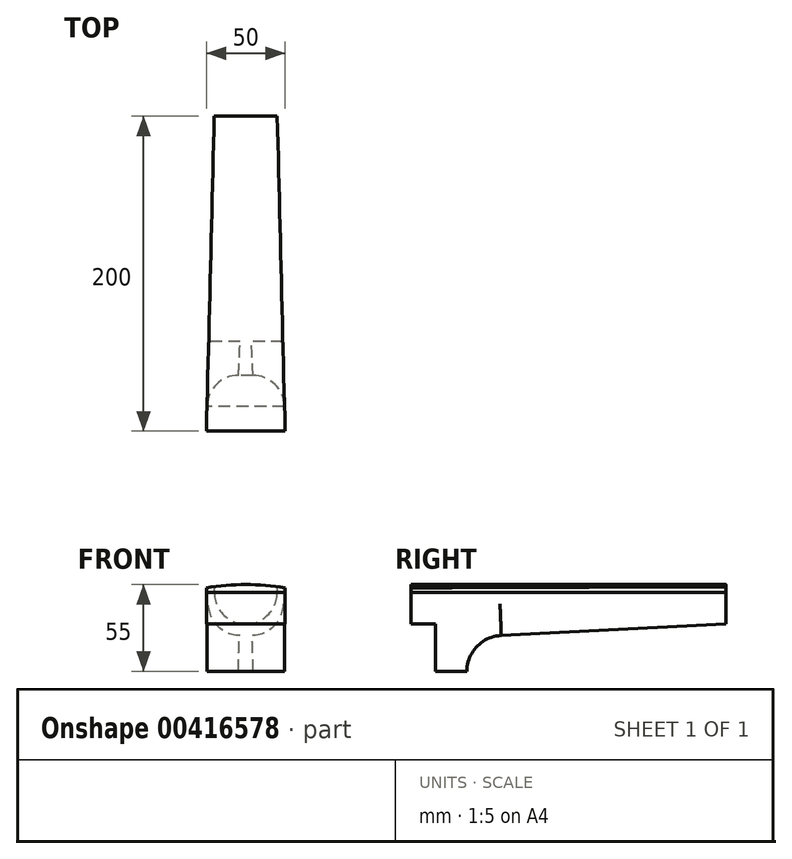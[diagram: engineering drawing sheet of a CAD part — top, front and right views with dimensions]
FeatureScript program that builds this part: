
annotation { "Feature Type Name" : "Feature", "Feature Type Description" : "" }
export const myFeature = defineFeature(function(context is Context, id is Id, definition is map)
    precondition{}
    {
        {
            var Q0;
            Q0=qCreatedBy(makeId("Front.planeOp"),FACE);
            var sketch = newSketch(context, id + "F0", { "sketchPlane" : qUnion([Q0])});
            skLineSegment(sketch, "E0.bottom", {"start": v(25, 25) * mm, "end": v(-25, 25) * mm});
            skLineSegment(sketch, "E0.top", {"start": v(25, -25) * mm, "end": v(-25, -25) * mm});
            skLineSegment(sketch, "E0.left", {"start": v(25, 25) * mm, "end": v(25, -25) * mm});
            skLineSegment(sketch, "E0.right", {"start": v(-25, 25) * mm, "end": v(-25, -25) * mm});
            skPoint(sketch, "E0.middle", {"position": v(0, 0) * mm});
            skSolve(sketch);
        }
        {
            var Q0;
            Q0 = qSketchRegion(id + "F0", true);
            extrude(context, id + "F1", {"entities" : qUnion([Q0]), "depth" : 200 * mm, "symmetric" : true});
        }
        {
            var Q0;
            Q0=qCreatedBy(makeId("Right.planeOp"),FACE);
            var sketch = newSketch(context, id + "F2", { "sketchPlane" : qUnion([Q0])});
            skLineSegment(sketch, "E1", {"start": v(100, 5) * mm, "end": v(-43.03, -2.33) * mm});
            skArc(sketch, "E2", {"start": v(-43.03, -2.33) * mm, "mid": v(-58.32, -9.37) * mm, "end": v(-64.56, -25) * mm});
            skLineSegment(sketch, "E3", {"start": v(100, 5) * mm, "end": v(100, -25) * mm});
            skLineSegment(sketch, "E4", {"start": v(-64.56, -25) * mm, "end": v(100, -25) * mm});
            skSolve(sketch);
        }
        {
            var Q0;
            Q0 = qSketchRegion(id + "F2", true);
            extrude(context, id + "F3", {"entities" : qUnion([Q0]), "operationType" : NewBodyOperationType.REMOVE, "depth" : 100 * mm, "symmetric" : true});
        }
        {
            var Q0;
            Q0=makeQuery(id+"F1.opExtrude","SWEPT_FACE",FACE,{"disambiguationData":[OSD([sQuery(id+"F0.wireOp",EDGE,"E0.bottom")])]});
            var sketch = newSketch(context, id + "F4", { "sketchPlane" : qUnion([Q0])});
            skLineSegment(sketch, "E5", {"start": v(-25, -100) * mm, "end": v(-20, 100) * mm});
            skLineSegment(sketch, "E6", {"start": v(-20, 100) * mm, "end": v(-25, 100) * mm});
            skLineSegment(sketch, "E7.MirrorCS", {"start": v(25, -100) * mm, "end": v(20, 100) * mm});
            skSolve(sketch);
        }
        {
            var Q0;
            {var subQ0=sQuery(id+"F4.wireOp",EDGE,"E7.MirrorCS");Q0=makeQuery(id+"F4.imprint","IMPRINT",FACE,{"disambiguationData":[TD([[makeQuery(id+"F4.imprint","IMPRINT",EDGE,{"derivedFrom":subQ0}),-1.0]])]});}
            var Q1;
            Q1=makeQuery(id+"F4.imprint","IMPRINT",FACE,{"disambiguationData":[TD([[makeQuery(id+"F4.imprint","IMPRINT",EDGE,{"derivedFrom":sQuery(id+"F4.wireOp",EDGE,"E5")}),1.0]])]});
            extrude(context, id + "F5", {"entities" : qUnion([Q0, Q1]), "operationType" : NewBodyOperationType.REMOVE, "oppositeDirection" : true, "depth" : 100 * mm});
        }
        {
            var Q0;
            Q0=makeQuery(id+"F5.boolean.opBoolean","INTERSECT",EDGE,{"derivedFrom":[makeQuery(id+"F3.boolean.opBoolean","COPY",FACE,{"derivedFrom":makeQuery(id+"F3.opExtrude","SWEPT_FACE",FACE,{"disambiguationData":[OSD([sQuery(id+"F2.wireOp",EDGE,"E2")])]})}),makeQuery(id+"F5.opExtrude","SWEPT_FACE",FACE,{"disambiguationData":[OSD([sQuery(id+"F4.wireOp",EDGE,"E5")])]})]});
            var Q1;
            Q1=makeQuery(id+"F5.boolean.opBoolean","INTERSECT",EDGE,{"derivedFrom":[makeQuery(id+"F3.boolean.opBoolean","COPY",FACE,{"derivedFrom":makeQuery(id+"F3.opExtrude","SWEPT_FACE",FACE,{"disambiguationData":[OSD([sQuery(id+"F2.wireOp",EDGE,"E1")])]})}),makeQuery(id+"F5.opExtrude","SWEPT_FACE",FACE,{"disambiguationData":[OSD([sQuery(id+"F4.wireOp",EDGE,"E5")])]})]});
            var Q2;
            Q2=makeQuery(id+"F5.boolean.opBoolean","INTERSECT",EDGE,{"derivedFrom":[makeQuery(id+"F3.boolean.opBoolean","COPY",FACE,{"derivedFrom":makeQuery(id+"F3.opExtrude","SWEPT_FACE",FACE,{"disambiguationData":[OSD([sQuery(id+"F2.wireOp",EDGE,"E2")])]})}),makeQuery(id+"F5.opExtrude","SWEPT_FACE",FACE,{"disambiguationData":[OSD([sQuery(id+"F4.wireOp",EDGE,"E7.MirrorCS")])]})]});
            var Q3;
            Q3=makeQuery(id+"F5.boolean.opBoolean","INTERSECT",EDGE,{"derivedFrom":[makeQuery(id+"F3.boolean.opBoolean","COPY",FACE,{"derivedFrom":makeQuery(id+"F3.opExtrude","SWEPT_FACE",FACE,{"disambiguationData":[OSD([sQuery(id+"F2.wireOp",EDGE,"E1")])]})}),makeQuery(id+"F5.opExtrude","SWEPT_FACE",FACE,{"disambiguationData":[OSD([sQuery(id+"F4.wireOp",EDGE,"E7.MirrorCS")])]})]});
            fillet(context, id + "F6", {"entities" : qUnion([Q0, Q1, Q2, Q3]), "radius" : 20 * mm, "tangentPropagation" : true, "allowEdgeOverflow" : false});
        }
        {
            var Q0;
            Q0=makeQuery(id+"F1.opExtrude","CAP_FACE",FACE,{"disambiguationData":[OSD([sQuery(id+"F0.wireOp",EDGE,"E0.bottom"),sQuery(id+"F0.wireOp",EDGE,"E0.top"),sQuery(id+"F0.wireOp",EDGE,"E0.left"),sQuery(id+"F0.wireOp",EDGE,"E0.right")])],"isStart":false});
            var sketch = newSketch(context, id + "F7", { "sketchPlane" : qUnion([Q0])});
            skLineSegment(sketch, "E8.bottom", {"start": v(-49.86, 5) * mm, "end": v(38.41, 5) * mm});
            skLineSegment(sketch, "E8.top", {"start": v(-49.86, -46.51) * mm, "end": v(38.41, -46.51) * mm});
            skLineSegment(sketch, "E8.left", {"start": v(-49.86, 5) * mm, "end": v(-49.86, -46.51) * mm});
            skLineSegment(sketch, "E8.right", {"start": v(38.41, 5) * mm, "end": v(38.41, -46.51) * mm});
            skSolve(sketch);
        }
        {
            var Q0;
            Q0=makeQuery(id+"F7.imprint","IMPRINT",FACE,{"disambiguationData":[TD([[makeQuery(id+"F7.imprint","IMPRINT",EDGE,{"derivedFrom":sQuery(id+"F7.wireOp",EDGE,"E8.top")}),1.0]])]});
            var Q1;
            {var subQ8=makeQuery(id+"F1.opExtrude","CAP_EDGE",EDGE,{"disambiguationData":[OSD([sQuery(id+"F0.wireOp",EDGE,"E0.top")])],"isStart":false});Q1=makeQuery(id+"F7.imprint","IMPRINT",FACE,{"disambiguationData":[TD([[makeQuery(id+"F7.imprint","IMPRINT",EDGE,{"derivedFrom":subQ8}),-1.0]])]});}
            var Q2;
            Q2=makeQuery(id+"F5.boolean.opBoolean","COPY",FACE,{"derivedFrom":makeQuery(id+"F5.opExtrude","SWEPT_FACE",FACE,{"disambiguationData":[OSD([sQuery(id+"F4.wireOp",EDGE,"E7.MirrorCS")])]})});
            extrude(context, id + "F8", {"entities" : qUnion([Q0, Q1, Q2]), "operationType" : NewBodyOperationType.REMOVE, "oppositeDirection" : true, "depth" : 15.52 * mm});
        }
        {
            var Q0;
            Q0=makeQuery(id+"F1.opExtrude","SWEPT_FACE",FACE,{"disambiguationData":[OSD([sQuery(id+"F0.wireOp",EDGE,"E0.bottom")])]});
            var sketch = newSketch(context, id + "F9", { "sketchPlane" : qUnion([Q0])});
            skLineSegment(sketch, "E9", {"start": v(25, -100) * mm, "end": v(-25, -100) * mm});
            skLineSegment(sketch, "E10", {"start": v(-25, -100) * mm, "end": v(-20, 100) * mm});
            skLineSegment(sketch, "E11", {"start": v(-20, 100) * mm, "end": v(20, 99.99) * mm});
            skLineSegment(sketch, "E12", {"start": v(20, 99.99) * mm, "end": v(25, -100) * mm});
            skSolve(sketch);
        }
        {
            var Q0;
            {var subQ3=sQuery(id+"F9.wireOp",EDGE,"E9");Q0=makeQuery(id+"F9.imprint","IMPRINT",FACE,{"disambiguationData":[TD([[makeQuery(id+"F9.imprint","IMPRINT",EDGE,{"derivedFrom":subQ3}),-1.0]])]});}
            extrude(context, id + "F10", {"entities" : qUnion([Q0]), "depth" : 5 * mm});
        }
        {
            var Q0;
            Q0=makeQuery(id+"F10.opExtrude","SWEPT_FACE",FACE,{"disambiguationData":[OSD([sQuery(id+"F9.wireOp",EDGE,"E9")])]});
            var sketch = newSketch(context, id + "F11", { "sketchPlane" : qUnion([Q0])});
            skArc(sketch, "E13", {"start": v(29.65, 27.09) * mm, "mid": v(-3.62, 29.96) * mm, "end": v(-36.7, 25.51) * mm});
            skLineSegment(sketch, "E14", {"start": v(-36.7, 25.51) * mm, "end": v(-40.05, 41.58) * mm});
            skLineSegment(sketch, "E15", {"start": v(-40.05, 41.58) * mm, "end": v(32.52, 41.58) * mm});
            skLineSegment(sketch, "E16", {"start": v(32.52, 41.58) * mm, "end": v(29.65, 27.09) * mm});
            skSolve(sketch);
        }
        {
            var Q0;
            Q0 = qSketchRegion(id + "F11", true);
            extrude(context, id + "F12", {"entities" : qUnion([Q0]), "operationType" : NewBodyOperationType.REMOVE, "oppositeDirection" : true, "depth" : 247.65 * mm});
        }
    });
